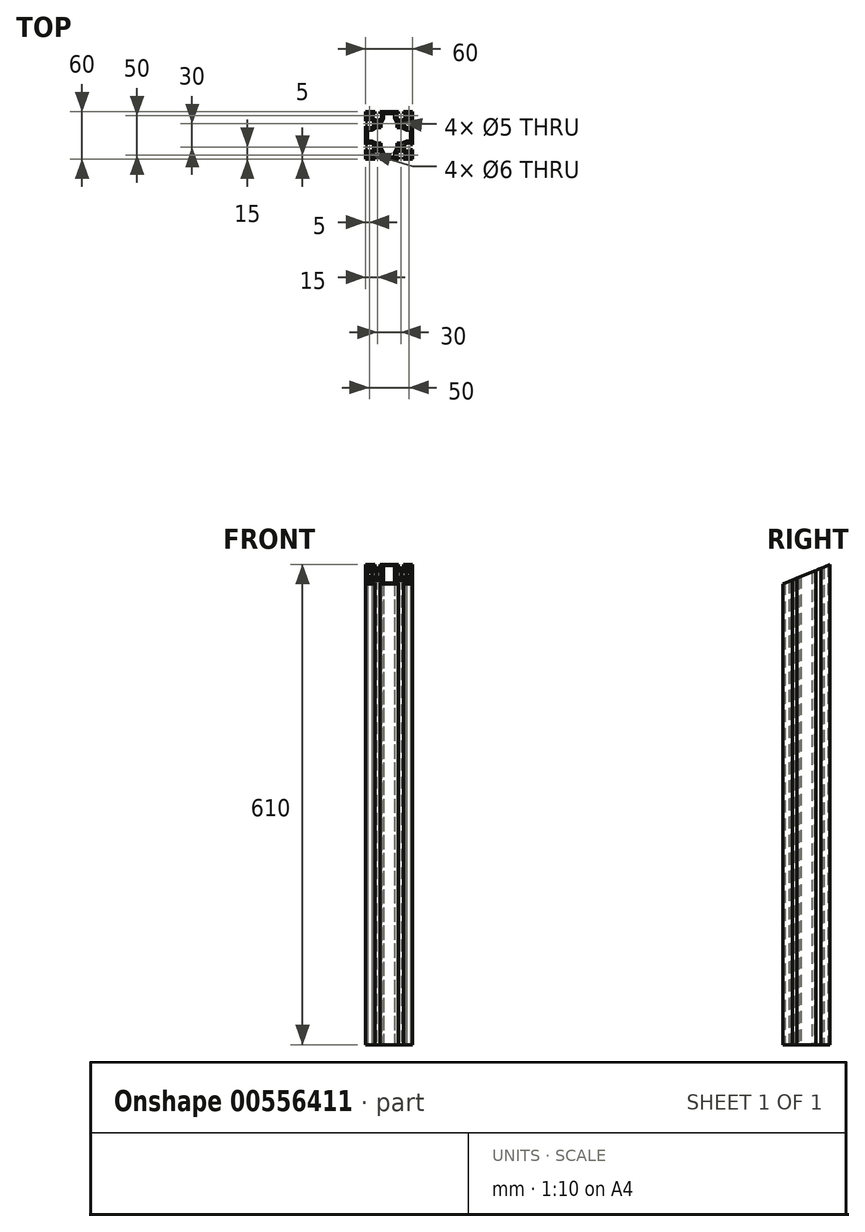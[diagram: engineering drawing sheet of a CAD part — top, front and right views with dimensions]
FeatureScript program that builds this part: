
annotation { "Feature Type Name" : "Feature", "Feature Type Description" : "" }
export const myFeature = defineFeature(function(context is Context, id is Id, definition is map)
    precondition{}
    {
        {
            var Q0;
            Q0=qCreatedBy(makeId("Top.planeOp"),FACE);
            var sketch = newSketch(context, id + "F0", { "sketchPlane" : qUnion([Q0])});
            skLineSegment(sketch, "E0.bottom", {"start": v(30, -30) * mm, "end": v(-30, -30) * mm});
            skLineSegment(sketch, "E0.top", {"start": v(30, 30) * mm, "end": v(-30, 30) * mm});
            skLineSegment(sketch, "E0.left", {"start": v(30, -30) * mm, "end": v(30, 30) * mm});
            skLineSegment(sketch, "E0.right", {"start": v(-30, -30) * mm, "end": v(-30, 30) * mm});
            skPoint(sketch, "E0.middle", {"position": v(0, 0) * mm});
            skLineSegment(sketch, "E1.top", {"start": v(-11.85, 30) * mm, "end": v(-18.15, 30) * mm});
            skLineSegment(sketch, "E1.left", {"start": v(-11.85, 27.5) * mm, "end": v(-11.85, 30) * mm});
            skLineSegment(sketch, "E1.right", {"start": v(-18.15, 27.5) * mm, "end": v(-18.15, 30) * mm});
            skPoint(sketch, "E1.middle", {"position": v(-15, 28.75) * mm});
            skLineSegment(sketch, "E2.bottom", {"start": v(-9.85, 27.5) * mm, "end": v(-11.85, 27.5) * mm});
            skLineSegment(sketch, "E2.left", {"start": v(-9.85, 27.5) * mm, "end": v(-9.85, 21.55) * mm});
            skLineSegment(sketch, "E2.right", {"start": v(-20.15, 27.5) * mm, "end": v(-20.15, 21.55) * mm});
            skPoint(sketch, "E2.middle", {"position": v(-15, 24.52) * mm});
            skArc(sketch, "E3", {"start": v(-20.15, 21.55) * mm, "mid": v(-15, 19.5) * mm, "end": v(-9.85, 21.55) * mm});
            skPoint(sketch, "E4.MirrorP", {"position": v(15, 24.52) * mm});
            skPoint(sketch, "E5.MirrorP", {"position": v(15, 28.75) * mm});
            skLineSegment(sketch, "E6.MirrorCS", {"start": v(11.85, 27.5) * mm, "end": v(11.85, 30) * mm});
            skLineSegment(sketch, "E7.MirrorCS", {"start": v(18.15, 27.5) * mm, "end": v(18.15, 30) * mm});
            skLineSegment(sketch, "E8.MirrorCS", {"start": v(9.85, 27.5) * mm, "end": v(11.85, 27.5) * mm});
            skLineSegment(sketch, "E9.MirrorCS", {"start": v(9.85, 27.5) * mm, "end": v(9.85, 21.55) * mm});
            skArc(sketch, "E10.MirrorCS", {"start": v(20.15, 21.55) * mm, "mid": v(15, 19.5) * mm, "end": v(9.85, 21.55) * mm});
            skLineSegment(sketch, "E11.MirrorCS", {"start": v(20.15, 27.5) * mm, "end": v(20.15, 21.55) * mm});
            skLineSegment(sketch, "E12.MirrorCS", {"start": v(11.85, 30) * mm, "end": v(18.15, 30) * mm});
            skLineSegment(sketch, "E13.1.0", {"start": v(27.5, 20.15) * mm, "end": v(21.55, 20.15) * mm});
            skLineSegment(sketch, "E13.1.1", {"start": v(27.5, 9.85) * mm, "end": v(21.55, 9.85) * mm});
            skArc(sketch, "E13.1.2", {"start": v(21.55, 20.15) * mm, "mid": v(19.5, 15) * mm, "end": v(21.55, 9.85) * mm});
            skLineSegment(sketch, "E13.1.3", {"start": v(27.5, -9.85) * mm, "end": v(21.55, -9.85) * mm});
            skLineSegment(sketch, "E13.1.4", {"start": v(27.5, -20.15) * mm, "end": v(21.55, -20.15) * mm});
            skPoint(sketch, "E13.1.5", {"position": v(28.75, 15) * mm});
            skPoint(sketch, "E13.1.6", {"position": v(28.75, -15) * mm});
            skArc(sketch, "E13.1.7", {"start": v(21.55, -20.15) * mm, "mid": v(19.5, -15) * mm, "end": v(21.55, -9.85) * mm});
            skPoint(sketch, "E13.1.8", {"position": v(24.52, -15) * mm});
            skPoint(sketch, "E13.1.9", {"position": v(24.52, 15) * mm});
            skLineSegment(sketch, "E13.1.10", {"start": v(27.5, 9.85) * mm, "end": v(27.5, 20.15) * mm});
            skLineSegment(sketch, "E13.1.11", {"start": v(27.5, -11.85) * mm, "end": v(27.5, -18.15) * mm});
            skLineSegment(sketch, "E13.1.12", {"start": v(30, 11.85) * mm, "end": v(30, 18.15) * mm});
            skLineSegment(sketch, "E13.1.13", {"start": v(30, -11.85) * mm, "end": v(30, -18.15) * mm});
            skLineSegment(sketch, "E13.1.14", {"start": v(27.5, 18.15) * mm, "end": v(30, 18.15) * mm});
            skLineSegment(sketch, "E13.1.15", {"start": v(27.5, 11.85) * mm, "end": v(30, 11.85) * mm});
            skLineSegment(sketch, "E13.1.16", {"start": v(27.5, 11.85) * mm, "end": v(27.5, 18.15) * mm});
            skLineSegment(sketch, "E13.1.17", {"start": v(27.5, -9.85) * mm, "end": v(27.5, -20.15) * mm});
            skLineSegment(sketch, "E13.1.18", {"start": v(27.5, -18.15) * mm, "end": v(30, -18.15) * mm});
            skLineSegment(sketch, "E13.1.19", {"start": v(27.5, -11.85) * mm, "end": v(30, -11.85) * mm});
            skLineSegment(sketch, "E13.2.0", {"start": v(20.15, -27.5) * mm, "end": v(20.15, -21.55) * mm});
            skLineSegment(sketch, "E13.2.1", {"start": v(9.85, -27.5) * mm, "end": v(9.85, -21.55) * mm});
            skArc(sketch, "E13.2.2", {"start": v(20.15, -21.55) * mm, "mid": v(15, -19.5) * mm, "end": v(9.85, -21.55) * mm});
            skLineSegment(sketch, "E13.2.3", {"start": v(-9.85, -27.5) * mm, "end": v(-9.85, -21.55) * mm});
            skLineSegment(sketch, "E13.2.4", {"start": v(-20.15, -27.5) * mm, "end": v(-20.15, -21.55) * mm});
            skPoint(sketch, "E13.2.5", {"position": v(15, -28.75) * mm});
            skPoint(sketch, "E13.2.6", {"position": v(-15, -28.75) * mm});
            skArc(sketch, "E13.2.7", {"start": v(-20.15, -21.55) * mm, "mid": v(-15, -19.5) * mm, "end": v(-9.85, -21.55) * mm});
            skPoint(sketch, "E13.2.8", {"position": v(-15, -24.52) * mm});
            skPoint(sketch, "E13.2.9", {"position": v(15, -24.52) * mm});
            skLineSegment(sketch, "E13.2.10", {"start": v(9.85, -27.5) * mm, "end": v(20.15, -27.5) * mm});
            skLineSegment(sketch, "E13.2.11", {"start": v(-11.85, -27.5) * mm, "end": v(-18.15, -27.5) * mm});
            skLineSegment(sketch, "E13.2.12", {"start": v(11.85, -30) * mm, "end": v(18.15, -30) * mm});
            skLineSegment(sketch, "E13.2.13", {"start": v(-11.85, -30) * mm, "end": v(-18.15, -30) * mm});
            skLineSegment(sketch, "E13.2.14", {"start": v(18.15, -27.5) * mm, "end": v(18.15, -30) * mm});
            skLineSegment(sketch, "E13.2.15", {"start": v(11.85, -27.5) * mm, "end": v(11.85, -30) * mm});
            skLineSegment(sketch, "E13.2.16", {"start": v(11.85, -27.5) * mm, "end": v(18.15, -27.5) * mm});
            skLineSegment(sketch, "E13.2.17", {"start": v(-9.85, -27.5) * mm, "end": v(-20.15, -27.5) * mm});
            skLineSegment(sketch, "E13.2.18", {"start": v(-18.15, -27.5) * mm, "end": v(-18.15, -30) * mm});
            skLineSegment(sketch, "E13.2.19", {"start": v(-11.85, -27.5) * mm, "end": v(-11.85, -30) * mm});
            skLineSegment(sketch, "E13.3.0", {"start": v(-27.5, -20.15) * mm, "end": v(-21.55, -20.15) * mm});
            skLineSegment(sketch, "E13.3.1", {"start": v(-27.5, -9.85) * mm, "end": v(-21.55, -9.85) * mm});
            skArc(sketch, "E13.3.2", {"start": v(-21.55, -20.15) * mm, "mid": v(-19.5, -15) * mm, "end": v(-21.55, -9.85) * mm});
            skLineSegment(sketch, "E13.3.3", {"start": v(-27.5, 9.85) * mm, "end": v(-21.55, 9.85) * mm});
            skLineSegment(sketch, "E13.3.4", {"start": v(-27.5, 20.15) * mm, "end": v(-21.55, 20.15) * mm});
            skPoint(sketch, "E13.3.5", {"position": v(-28.75, -15) * mm});
            skPoint(sketch, "E13.3.6", {"position": v(-28.75, 15) * mm});
            skArc(sketch, "E13.3.7", {"start": v(-21.55, 20.15) * mm, "mid": v(-19.5, 15) * mm, "end": v(-21.55, 9.85) * mm});
            skPoint(sketch, "E13.3.8", {"position": v(-24.52, 15) * mm});
            skPoint(sketch, "E13.3.9", {"position": v(-24.52, -15) * mm});
            skLineSegment(sketch, "E13.3.10", {"start": v(-27.5, -9.85) * mm, "end": v(-27.5, -20.15) * mm});
            skLineSegment(sketch, "E13.3.11", {"start": v(-27.5, 11.85) * mm, "end": v(-27.5, 18.15) * mm});
            skLineSegment(sketch, "E13.3.12", {"start": v(-30, -11.85) * mm, "end": v(-30, -18.15) * mm});
            skLineSegment(sketch, "E13.3.13", {"start": v(-30, 11.85) * mm, "end": v(-30, 18.15) * mm});
            skLineSegment(sketch, "E13.3.14", {"start": v(-27.5, -18.15) * mm, "end": v(-30, -18.15) * mm});
            skLineSegment(sketch, "E13.3.15", {"start": v(-27.5, -11.85) * mm, "end": v(-30, -11.85) * mm});
            skLineSegment(sketch, "E13.3.16", {"start": v(-27.5, -11.85) * mm, "end": v(-27.5, -18.15) * mm});
            skLineSegment(sketch, "E13.3.17", {"start": v(-27.5, 9.85) * mm, "end": v(-27.5, 20.15) * mm});
            skLineSegment(sketch, "E13.3.18", {"start": v(-27.5, 18.15) * mm, "end": v(-30, 18.15) * mm});
            skLineSegment(sketch, "E13.3.19", {"start": v(-27.5, 11.85) * mm, "end": v(-30, 11.85) * mm});
            skLineSegment(sketch, "E13.anchor1", {"start": v(0, 0) * mm, "end": v(-20.15, 21.55) * mm, "construction": true});
            skLineSegment(sketch, "E13.anchor2", {"start": v(0, 0) * mm, "end": v(-21.55, -20.15) * mm, "construction": true});
            skLineSegment(sketch, "E14.trimOffspring", {"start": v(-18.15, 27.5) * mm, "end": v(-20.15, 27.5) * mm});
            skLineSegment(sketch, "E15.trimOffspring", {"start": v(18.15, 27.5) * mm, "end": v(20.15, 27.5) * mm});
            skCircle(sketch, "E16", {"center": v(-15, 15) * mm, "radius": 2.5 * mm});
            skCircle(sketch, "E17", {"center": v(-25, 25) * mm, "radius": 3 * mm});
            skCircle(sketch, "E18.MirrorC", {"center": v(25, 25) * mm, "radius": 3 * mm});
            skCircle(sketch, "E19.MirrorC", {"center": v(25, -25) * mm, "radius": 3 * mm});
            skCircle(sketch, "E20.MirrorC", {"center": v(-25, -25) * mm, "radius": 3 * mm});
            skCircle(sketch, "E21.MirrorC", {"center": v(15, 15) * mm, "radius": 2.5 * mm});
            skCircle(sketch, "E22.MirrorC", {"center": v(15, -15) * mm, "radius": 2.5 * mm});
            skCircle(sketch, "E23.MirrorC", {"center": v(-15, -15) * mm, "radius": 2.5 * mm});
            skLineSegment(sketch, "E24", {"start": v(-7, 27.5) * mm, "end": v(0, 27.5) * mm});
            skLineSegment(sketch, "E25", {"start": v(-7, 27.5) * mm, "end": v(-7, 22) * mm});
            skLineSegment(sketch, "E26", {"start": v(-10, 10) * mm, "end": v(-10, 16) * mm});
            skLineSegment(sketch, "E27", {"start": v(-10, 16) * mm, "end": v(-7, 22) * mm});
            skLineSegment(sketch, "E28.MirrorCS", {"start": v(10, 10) * mm, "end": v(10, 16) * mm});
            skLineSegment(sketch, "E29.MirrorCS", {"start": v(10, 16) * mm, "end": v(7, 22) * mm});
            skLineSegment(sketch, "E30.MirrorCS", {"start": v(7, 27.5) * mm, "end": v(0, 27.5) * mm});
            skLineSegment(sketch, "E31.MirrorCS", {"start": v(7, 27.5) * mm, "end": v(7, 22) * mm});
            skLineSegment(sketch, "E32.1.0", {"start": v(-10, -10) * mm, "end": v(-16, -10) * mm});
            skLineSegment(sketch, "E32.1.1", {"start": v(-16, -10) * mm, "end": v(-22, -7) * mm});
            skLineSegment(sketch, "E32.1.2", {"start": v(-27.5, -7) * mm, "end": v(-22, -7) * mm});
            skLineSegment(sketch, "E32.1.3", {"start": v(-27.5, -7) * mm, "end": v(-27.5, 0) * mm});
            skLineSegment(sketch, "E32.1.4", {"start": v(-27.5, 7) * mm, "end": v(-27.5, 0) * mm});
            skLineSegment(sketch, "E32.1.5", {"start": v(-27.5, 7) * mm, "end": v(-22, 7) * mm});
            skLineSegment(sketch, "E32.1.6", {"start": v(-16, 10) * mm, "end": v(-22, 7) * mm});
            skLineSegment(sketch, "E32.1.7", {"start": v(-10, 10) * mm, "end": v(-16, 10) * mm});
            skLineSegment(sketch, "E32.2.0", {"start": v(10, -10) * mm, "end": v(10, -16) * mm});
            skLineSegment(sketch, "E32.2.1", {"start": v(10, -16) * mm, "end": v(7, -22) * mm});
            skLineSegment(sketch, "E32.2.2", {"start": v(7, -27.5) * mm, "end": v(7, -22) * mm});
            skLineSegment(sketch, "E32.2.3", {"start": v(7, -27.5) * mm, "end": v(0, -27.5) * mm});
            skLineSegment(sketch, "E32.2.4", {"start": v(-7, -27.5) * mm, "end": v(0, -27.5) * mm});
            skLineSegment(sketch, "E32.2.5", {"start": v(-7, -27.5) * mm, "end": v(-7, -22) * mm});
            skLineSegment(sketch, "E32.2.6", {"start": v(-10, -16) * mm, "end": v(-7, -22) * mm});
            skLineSegment(sketch, "E32.2.7", {"start": v(-10, -10) * mm, "end": v(-10, -16) * mm});
            skLineSegment(sketch, "E32.3.0", {"start": v(10, 10) * mm, "end": v(16, 10) * mm});
            skLineSegment(sketch, "E32.3.1", {"start": v(16, 10) * mm, "end": v(22, 7) * mm});
            skLineSegment(sketch, "E32.3.2", {"start": v(27.5, 7) * mm, "end": v(22, 7) * mm});
            skLineSegment(sketch, "E32.3.3", {"start": v(27.5, 7) * mm, "end": v(27.5, 0) * mm});
            skLineSegment(sketch, "E32.3.4", {"start": v(27.5, -7) * mm, "end": v(27.5, 0) * mm});
            skLineSegment(sketch, "E32.3.5", {"start": v(27.5, -7) * mm, "end": v(22, -7) * mm});
            skLineSegment(sketch, "E32.3.6", {"start": v(16, -10) * mm, "end": v(22, -7) * mm});
            skLineSegment(sketch, "E32.3.7", {"start": v(10, -10) * mm, "end": v(16, -10) * mm});
            skSolve(sketch);
        }
        {
            var Q0;
            {var subQ30=sQuery(id+"F0.wireOp",EDGE,"E1.left");Q0=makeQuery(id+"F0.imprint","IMPRINT",FACE,{"disambiguationData":[TD([[makeQuery(id+"F0.imprint","IMPRINT",EDGE,{"derivedFrom":subQ30}),-1.0]])]});}
            extrude(context, id + "F1", {"entities" : qUnion([Q0]), "depth" : 610 * mm, "offsetDistance" : 25 * mm});
        }
        {
            var Q0;
            Q0=makeQuery(id+"F1.opExtrude","SWEPT_EDGE",EDGE,{"disambiguationData":[OSD([sQuery(id+"F0.wireOp",EDGE,"E24"),sQuery(id+"F0.wireOp",EDGE,"E25")])]});
            var Q1;
            Q1=makeQuery(id+"F1.opExtrude","SWEPT_EDGE",EDGE,{"disambiguationData":[OSD([sQuery(id+"F0.wireOp",EDGE,"E30.MirrorCS"),sQuery(id+"F0.wireOp",EDGE,"E31.MirrorCS")])]});
            var Q2;
            Q2=makeQuery(id+"F1.opExtrude","SWEPT_EDGE",EDGE,{"disambiguationData":[OSD([sQuery(id+"F0.wireOp",EDGE,"840db5bc-c403-45cd-90c7-254e62d9e8c5.3.2"),sQuery(id+"F0.wireOp",EDGE,"840db5bc-c403-45cd-90c7-254e62d9e8c5.3.3")])]});
            var Q3;
            Q3=makeQuery(id+"F1.opExtrude","SWEPT_EDGE",EDGE,{"disambiguationData":[OSD([sQuery(id+"F0.wireOp",EDGE,"840db5bc-c403-45cd-90c7-254e62d9e8c5.3.4"),sQuery(id+"F0.wireOp",EDGE,"840db5bc-c403-45cd-90c7-254e62d9e8c5.3.5")])]});
            var Q4;
            Q4=makeQuery(id+"F1.opExtrude","SWEPT_EDGE",EDGE,{"disambiguationData":[OSD([sQuery(id+"F0.wireOp",EDGE,"840db5bc-c403-45cd-90c7-254e62d9e8c5.1.4"),sQuery(id+"F0.wireOp",EDGE,"840db5bc-c403-45cd-90c7-254e62d9e8c5.1.5")])]});
            var Q5;
            Q5=makeQuery(id+"F1.opExtrude","SWEPT_EDGE",EDGE,{"disambiguationData":[OSD([sQuery(id+"F0.wireOp",EDGE,"840db5bc-c403-45cd-90c7-254e62d9e8c5.1.2"),sQuery(id+"F0.wireOp",EDGE,"840db5bc-c403-45cd-90c7-254e62d9e8c5.1.3")])]});
            var Q6;
            Q6=makeQuery(id+"F1.opExtrude","SWEPT_EDGE",EDGE,{"disambiguationData":[OSD([sQuery(id+"F0.wireOp",EDGE,"840db5bc-c403-45cd-90c7-254e62d9e8c5.2.2"),sQuery(id+"F0.wireOp",EDGE,"840db5bc-c403-45cd-90c7-254e62d9e8c5.2.3")])]});
            var Q7;
            Q7=makeQuery(id+"F1.opExtrude","SWEPT_EDGE",EDGE,{"disambiguationData":[OSD([sQuery(id+"F0.wireOp",EDGE,"840db5bc-c403-45cd-90c7-254e62d9e8c5.2.4"),sQuery(id+"F0.wireOp",EDGE,"840db5bc-c403-45cd-90c7-254e62d9e8c5.2.5")])]});
            fillet(context, id + "F2", {"entities" : qUnion([Q0, Q1, Q2, Q3, Q4, Q5, Q6, Q7]), "radius" : 2 * mm, "tangentPropagation" : true, "allowEdgeOverflow" : false});
        }
        {
            var Q0;
            Q0=makeQuery(id+"F1.opExtrude","SWEPT_EDGE",EDGE,{"disambiguationData":[OSD([sQuery(id+"F0.wireOp",EDGE,"E26"),sQuery(id+"F0.wireOp",EDGE,"E27")])]});
            var Q1;
            Q1=makeQuery(id+"F1.opExtrude","SWEPT_EDGE",EDGE,{"disambiguationData":[OSD([sQuery(id+"F0.wireOp",EDGE,"E28.MirrorCS"),sQuery(id+"F0.wireOp",EDGE,"E29.MirrorCS")])]});
            var Q2;
            Q2=makeQuery(id+"F1.opExtrude","SWEPT_EDGE",EDGE,{"disambiguationData":[OSD([sQuery(id+"F0.wireOp",EDGE,"840db5bc-c403-45cd-90c7-254e62d9e8c5.3.0"),sQuery(id+"F0.wireOp",EDGE,"840db5bc-c403-45cd-90c7-254e62d9e8c5.3.1")])]});
            var Q3;
            Q3=makeQuery(id+"F1.opExtrude","SWEPT_EDGE",EDGE,{"disambiguationData":[OSD([sQuery(id+"F0.wireOp",EDGE,"840db5bc-c403-45cd-90c7-254e62d9e8c5.1.6"),sQuery(id+"F0.wireOp",EDGE,"840db5bc-c403-45cd-90c7-254e62d9e8c5.1.7")])]});
            var Q4;
            Q4=makeQuery(id+"F1.opExtrude","SWEPT_EDGE",EDGE,{"disambiguationData":[OSD([sQuery(id+"F0.wireOp",EDGE,"840db5bc-c403-45cd-90c7-254e62d9e8c5.1.0"),sQuery(id+"F0.wireOp",EDGE,"840db5bc-c403-45cd-90c7-254e62d9e8c5.1.1")])]});
            var Q5;
            Q5=makeQuery(id+"F1.opExtrude","SWEPT_EDGE",EDGE,{"disambiguationData":[OSD([sQuery(id+"F0.wireOp",EDGE,"840db5bc-c403-45cd-90c7-254e62d9e8c5.3.6"),sQuery(id+"F0.wireOp",EDGE,"840db5bc-c403-45cd-90c7-254e62d9e8c5.3.7")])]});
            var Q6;
            Q6=makeQuery(id+"F1.opExtrude","SWEPT_EDGE",EDGE,{"disambiguationData":[OSD([sQuery(id+"F0.wireOp",EDGE,"840db5bc-c403-45cd-90c7-254e62d9e8c5.2.0"),sQuery(id+"F0.wireOp",EDGE,"840db5bc-c403-45cd-90c7-254e62d9e8c5.2.1")])]});
            var Q7;
            Q7=makeQuery(id+"F1.opExtrude","SWEPT_EDGE",EDGE,{"disambiguationData":[OSD([sQuery(id+"F0.wireOp",EDGE,"840db5bc-c403-45cd-90c7-254e62d9e8c5.2.6"),sQuery(id+"F0.wireOp",EDGE,"840db5bc-c403-45cd-90c7-254e62d9e8c5.2.7")])]});
            fillet(context, id + "F3", {"entities" : qUnion([Q0, Q1, Q2, Q3, Q4, Q5, Q6, Q7]), "radius" : 7 * mm, "tangentPropagation" : true, "allowEdgeOverflow" : false});
        }
        {
            var Q0;
            Q0=qCreatedBy(makeId("Right.planeOp"),FACE);
            var sketch = newSketch(context, id + "F4", { "sketchPlane" : qUnion([Q0])});
            skLineSegment(sketch, "E33.bottom", {"start": v(-249.6, 768.34) * mm, "end": v(-66.93, 844) * mm});
            skLineSegment(sketch, "E33.top", {"start": v(-152.68, 534.33) * mm, "end": v(30, 610) * mm});
            skLineSegment(sketch, "E33.left", {"start": v(-249.6, 768.34) * mm, "end": v(-152.68, 534.33) * mm});
            skLineSegment(sketch, "E33.right", {"start": v(-66.93, 844) * mm, "end": v(30, 610) * mm});
            skSolve(sketch);
        }
        {
            var Q0;
            Q0=qSketchRegion(id+"F4",true);
            extrude(context, id + "F5", {"entities" : qUnion([Q0]), "operationType" : NewBodyOperationType.REMOVE, "depth" : 30 * mm, "offsetDistance" : 25 * mm, "hasSecondDirection" : true, "secondDirectionOppositeDirection" : true, "secondDirectionDepth" : 30 * mm});
        }
    });
